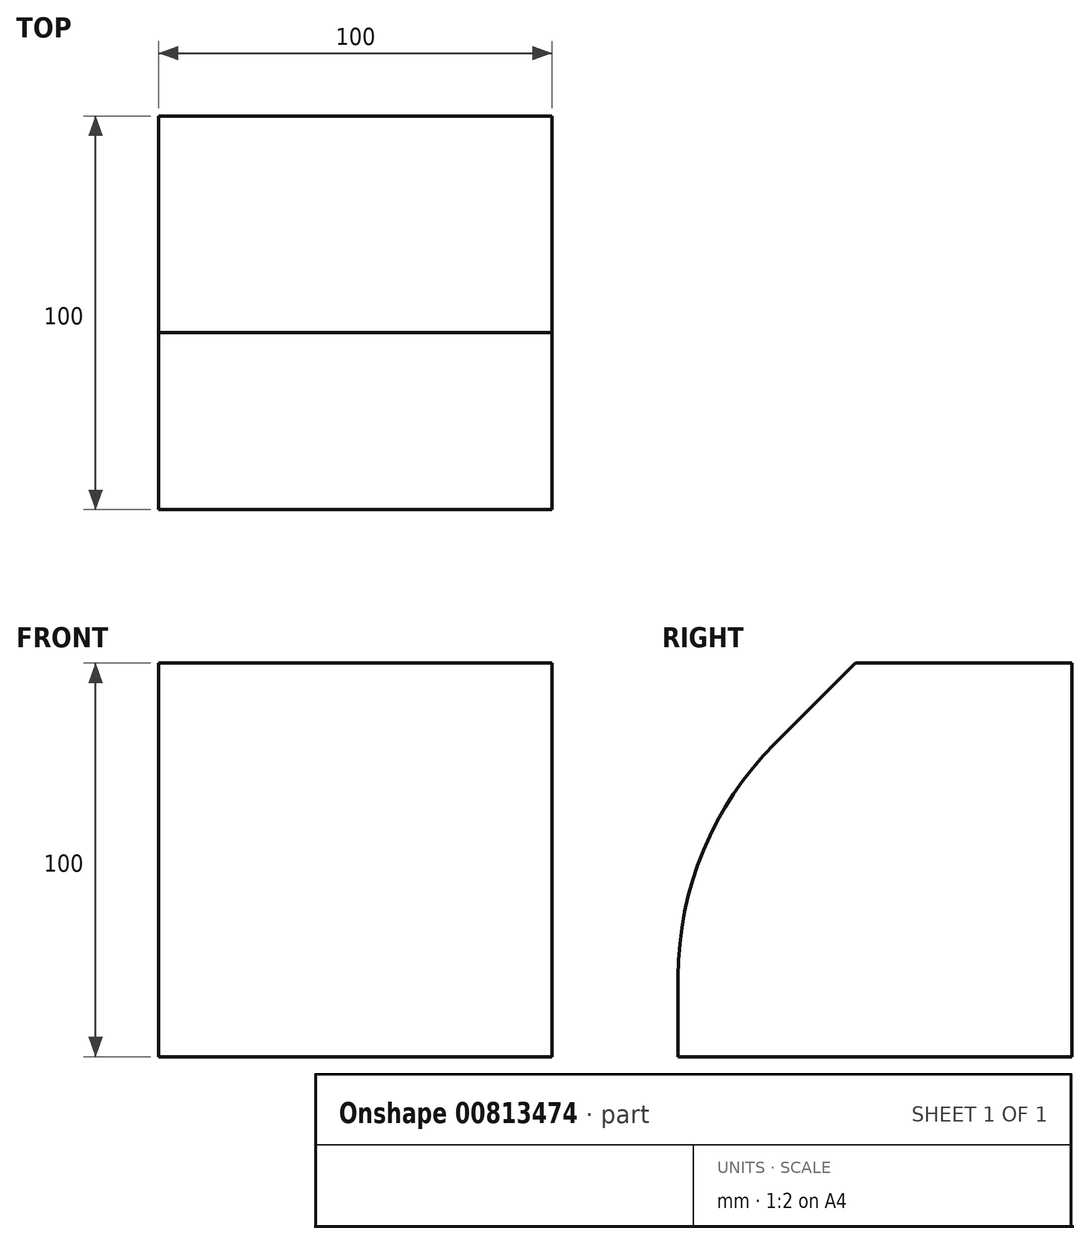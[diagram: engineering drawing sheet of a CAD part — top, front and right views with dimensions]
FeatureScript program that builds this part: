
annotation { "Feature Type Name" : "Feature", "Feature Type Description" : "" }
export const myFeature = defineFeature(function(context is Context, id is Id, definition is map)
    precondition{}
    {
        {
            var Q0;
            Q0=qCreatedBy(makeId("Top.planeOp"),FACE);
            var sketch = newSketch(context, id + "F0", { "sketchPlane" : qUnion([Q0])});
            skLineSegment(sketch, "E0.bottom", {"start": v(50, -50) * mm, "end": v(-50, -50) * mm});
            skLineSegment(sketch, "E0.top", {"start": v(50, 50) * mm, "end": v(-50, 50) * mm});
            skLineSegment(sketch, "E0.left", {"start": v(50, -50) * mm, "end": v(50, 50) * mm});
            skLineSegment(sketch, "E0.right", {"start": v(-50, -50) * mm, "end": v(-50, 50) * mm});
            skPoint(sketch, "E0.middle", {"position": v(0, 0) * mm});
            skSolve(sketch);
        }
        {
            var Q0;
            Q0=makeQuery(id+"F0.imprint","IMPRINT",FACE,{"disambiguationData":[TD([[makeQuery(id+"F0.imprint","IMPRINT",EDGE,{"derivedFrom":sQuery(id+"F0.wireOp",EDGE,"E0.bottom")}),-1.0]])]});
            extrude(context, id + "F1", {"entities" : qUnion([Q0]), "depth" : 100 * mm, "offsetDistance" : 25 * mm});
        }
        {
            var Q0;
            Q0=makeQuery(id+"F1.opExtrude","CAP_EDGE",EDGE,{"disambiguationData":[OSD([sQuery(id+"F0.wireOp",EDGE,"E0.bottom")])],"isStart":false});
            chamfer(context, id + "F2", {"entities" : qUnion([Q0]), "width" : 45 * mm, "tangentPropagation" : true});
        }
        {
            var Q0;
            {var subQ0=sQuery(id+"F0.wireOp",EDGE,"E0.bottom");Q0=makeQuery(id+"F2.opChamfer","BLEND_EDGE",EDGE,{"blendedFrom":[makeQuery(id+"F1.opExtrude","CAP_EDGE",EDGE,{"disambiguationData":[OSD([subQ0])],"isStart":false}),makeQuery(id+"F1.opExtrude","SWEPT_FACE",FACE,{"disambiguationData":[OSD([subQ0])]})],"blendedInto":[makeQuery(id+"F1.opExtrude","SWEPT_FACE",FACE,{"disambiguationData":[OSD([subQ0])]})]});}
            fillet(context, id + "F3", {"entities" : qUnion([Q0]), "radius" : 83.75 * mm, "tangentPropagation" : true, "allowEdgeOverflow" : false});
        }
    });
